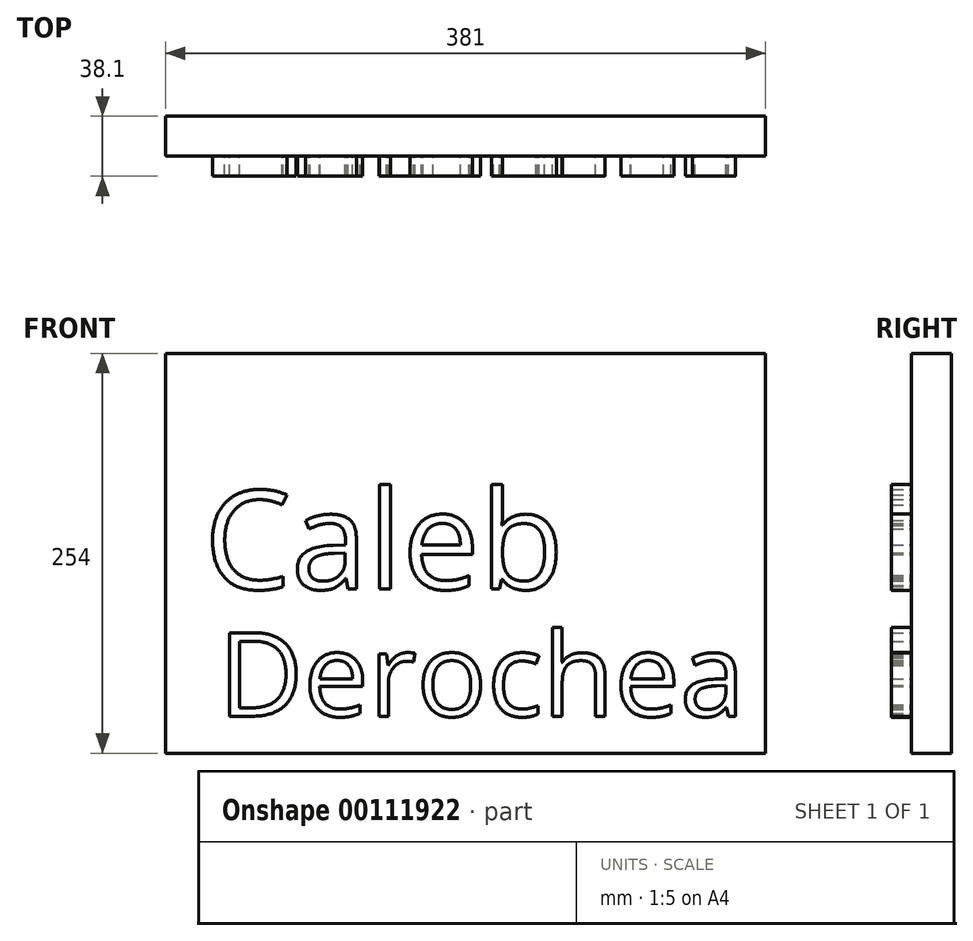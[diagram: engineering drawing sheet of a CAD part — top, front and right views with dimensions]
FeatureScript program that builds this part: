
annotation { "Feature Type Name" : "Feature", "Feature Type Description" : "" }
export const myFeature = defineFeature(function(context is Context, id is Id, definition is map)
    precondition{}
    {
        {
            var Q0;
            Q0=qCreatedBy(makeId("Front.planeOp"),FACE);
            var sketch = newSketch(context, id + "F0", { "sketchPlane" : qUnion([Q0])});
            skLineSegment(sketch, "E0.bottom", {"start": v(190.5, 127) * mm, "end": v(-190.5, 127) * mm});
            skLineSegment(sketch, "E0.top", {"start": v(190.5, -127) * mm, "end": v(-190.5, -127) * mm});
            skLineSegment(sketch, "E0.left", {"start": v(190.5, 127) * mm, "end": v(190.5, -127) * mm});
            skLineSegment(sketch, "E0.right", {"start": v(-190.5, 127) * mm, "end": v(-190.5, -127) * mm});
            skPoint(sketch, "E0.middle", {"position": v(0, 0) * mm});
            skSolve(sketch);
        }
        {
            var Q0;
            Q0 = qSketchRegion(id + "F0", true);
            extrude(context, id + "F1", {"entities" : qUnion([Q0]), "endBound" : BoundingType.SYMMETRIC, "oppositeDirection" : true, "depth" : 25.4 * mm});
        }
        {
            var Q0;
            Q0=makeQuery(id+"F1.opExtrude","CAP_FACE",FACE,{"disambiguationData":[OSD([sQuery(id+"F0.wireOp",EDGE,"E0.bottom"),sQuery(id+"F0.wireOp",EDGE,"E0.top"),sQuery(id+"F0.wireOp",EDGE,"E0.left"),sQuery(id+"F0.wireOp",EDGE,"E0.right")])],"isStart":true});
            var sketch = newSketch(context, id + "F2", { "sketchPlane" : qUnion([Q0])});
            skText(sketch, "E1", { "text": "Caleb", "fontName": "OpenSans-Regular.ttf"});
            const initialGuessF2  = {"E1": [-0.16602, -0.02271, 1, 0, 0.06294]};
            skSetInitialGuess(sketch, initialGuessF2);
            skSolve(sketch);
        }
        {
            var Q0;
            Q0 = qSketchRegion(id + "F2", true);
            extrude(context, id + "F4", {"entities" : qUnion([Q0]), "operationType" : NewBodyOperationType.ADD, "depth" : 12.7 * mm});
        }
        {
            var Q0;
            {var subQ0=sQuery(id+"F0.wireOp",EDGE,"E0.top");var subQ1=sQuery(id+"F0.wireOp",EDGE,"E0.right");var subQ2=sQuery(id+"F0.wireOp",EDGE,"E0.bottom");var subQ3=sQuery(id+"F0.wireOp",EDGE,"E0.left");Q0=makeQuery(id+"F4.boolean.opBoolean","SPLIT",FACE,{"disambiguationData":[TD([makeQuery(id+"F1.opExtrude","SWEPT_FACE",FACE,{"disambiguationData":[OSD([subQ2])]})])],"derivedFrom":makeQuery(id+"F1.opExtrude","CAP_FACE",FACE,{"disambiguationData":[OSD([subQ2,subQ0,subQ3,subQ1])],"isStart":true})});}
            var sketch = newSketch(context, id + "F5", { "sketchPlane" : qUnion([Q0])});
            skText(sketch, "E2", { "text": "Derochea", "fontName": "OpenSans-Regular.ttf"});
            const initialGuessFa0SdhMG0Q2AZoeFF_1  = {"E2": [-0.15708, -0.10347, 1, 0, 0.0534]};
            skSetInitialGuess(sketch, initialGuessFa0SdhMG0Q2AZoeFF_1);
            skSolve(sketch);
        }
        {
            var Q0;
            Q0 = qSketchRegion(id + "F5", true);
            extrude(context, id + "F3", {"entities" : qUnion([Q0]), "operationType" : NewBodyOperationType.ADD, "depth" : 12.7 * mm});
        }
    });
